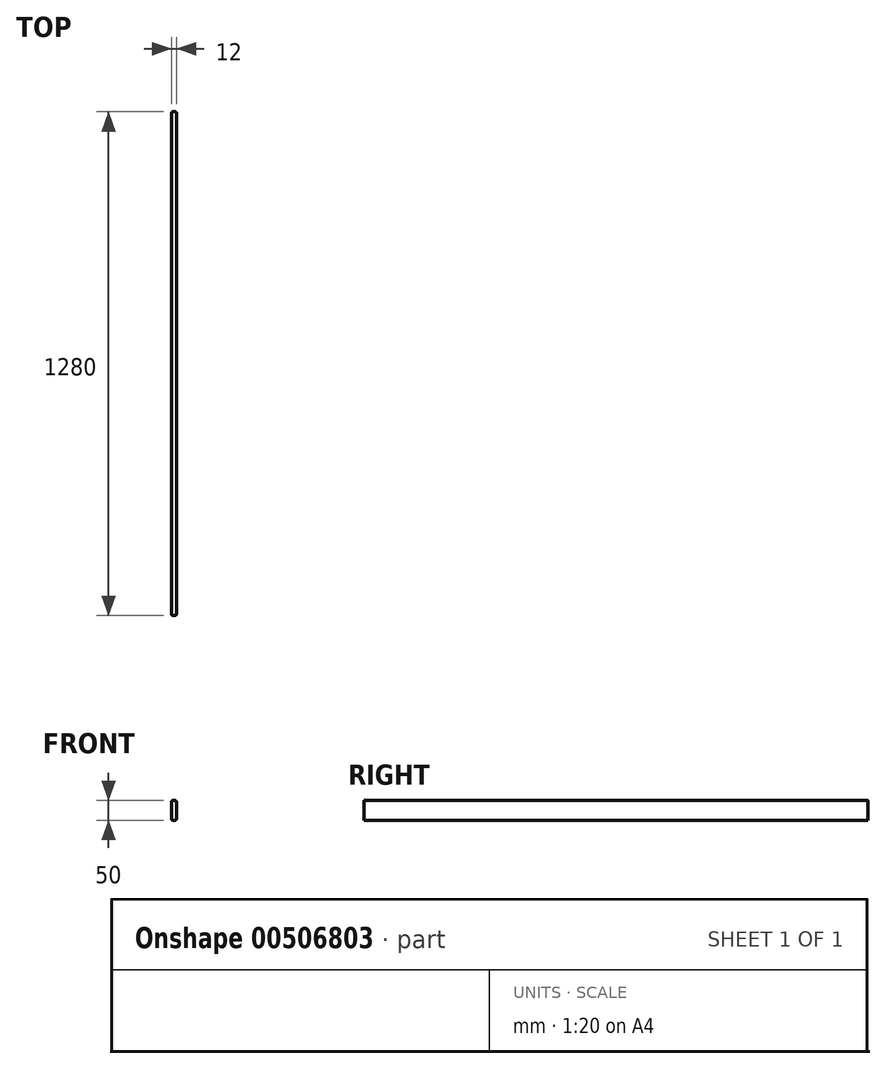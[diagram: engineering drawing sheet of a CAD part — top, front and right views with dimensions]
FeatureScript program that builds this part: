
annotation { "Feature Type Name" : "Feature", "Feature Type Description" : "" }
export const myFeature = defineFeature(function(context is Context, id is Id, definition is map)
    precondition{}
    {
        {
            var Q0;
            Q0=qCreatedBy(makeId("Front.planeOp"),FACE);
            var sketch = newSketch(context, id + "F0", { "sketchPlane" : qUnion([Q0])});
            skLineSegment(sketch, "E0.bottom", {"start": v(-116.2, 29.59) * mm, "end": v(-104.2, 29.59) * mm});
            skLineSegment(sketch, "E0.top", {"start": v(-116.2, -20.41) * mm, "end": v(-104.2, -20.41) * mm});
            skLineSegment(sketch, "E0.left", {"start": v(-116.2, 29.59) * mm, "end": v(-116.2, -20.41) * mm});
            skLineSegment(sketch, "E0.right", {"start": v(-104.2, 29.59) * mm, "end": v(-104.2, -20.41) * mm});
            skSolve(sketch);
        }
        {
            var Q0;
            Q0=makeQuery(id+"F0.imprint","IMPRINT",FACE,{"disambiguationData":[TD([[makeQuery(id+"F0.imprint","IMPRINT",EDGE,{"derivedFrom":sQuery(id+"F0.wireOp",EDGE,"E0.bottom")}),-1.0]])]});
            extrude(context, id + "F1", {"entities" : qUnion([Q0]), "depth" : 1280 * mm});
        }
        {
            var Q0;
            Q0=makeQuery(id+"F1.opExtrude","SWEPT_FACE",FACE,{"disambiguationData":[OSD([sQuery(id+"F0.wireOp",EDGE,"E0.left")])]});
            var sketch = newSketch(context, id + "F2", { "sketchPlane" : qUnion([Q0])});
            skLineSegment(sketch, "E1", {"start": v(1280, -20.41) * mm, "end": v(1280, -0.41) * mm});
            skLineSegment(sketch, "E2", {"start": v(1280, -0.41) * mm, "end": v(640, -0.41) * mm});
            skLineSegment(sketch, "E3", {"start": v(640, -0.41) * mm, "end": v(0, -0.41) * mm});
            skSolve(sketch);
        }
        {
            var Q0;
            Q0=makeQuery(id+"F1.opExtrude","SWEPT_FACE",FACE,{"disambiguationData":[OSD([sQuery(id+"F0.wireOp",EDGE,"E0.right")])]});
            var Q1;
            Q1=makeQuery(id+"F1.opExtrude","SWEPT_FACE",FACE,{"disambiguationData":[OSD([sQuery(id+"F0.wireOp",EDGE,"E0.left")])]});
            fillet(context, id + "F3", {"entities" : qUnion([Q0, Q1]), "radius" : 3 * mm, "tangentPropagation" : true, "allowEdgeOverflow" : false});
        }
    });
